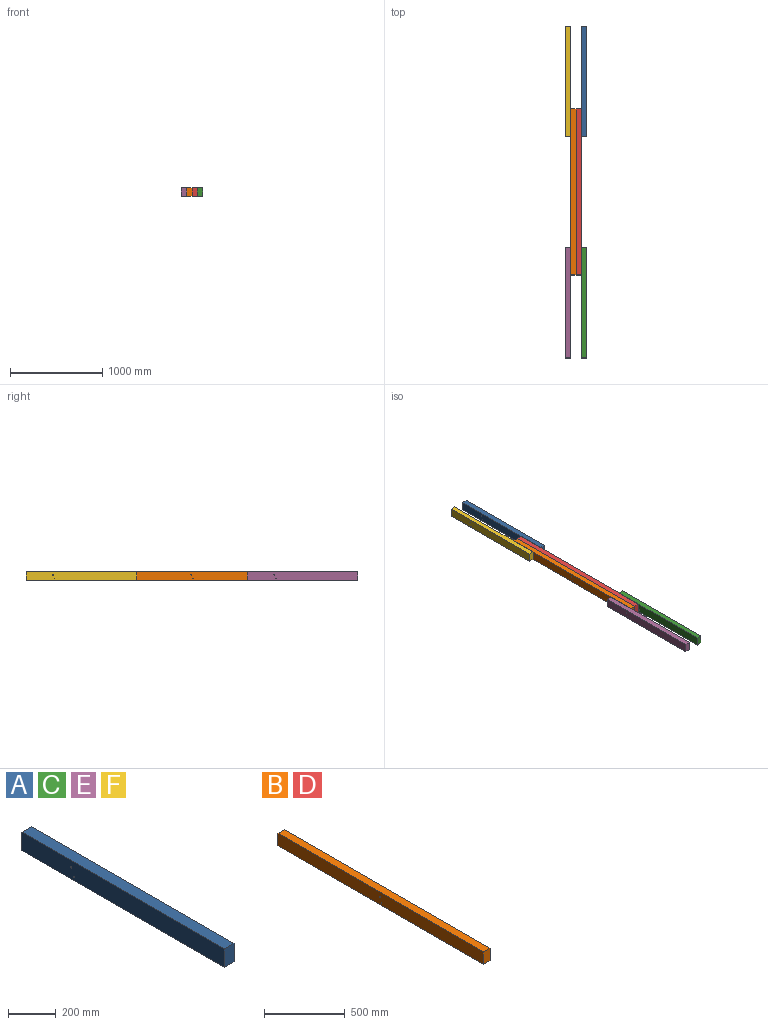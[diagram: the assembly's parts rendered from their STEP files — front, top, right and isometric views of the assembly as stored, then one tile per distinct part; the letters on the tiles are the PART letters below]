
ASSEMBLY  parts=6 mates=5
PART A: 8 faces, bbox 58x1200x95 mm
  f0: plane 1200x58mm, normal (0,0,-1), area 69600mm2, adj f1,f3,f4,f5
  f1: plane 1200x95mm, normal (1,0,0), area 113943.5mm2, adj f0,f2,f4,f5,f6,f7
  f2: plane 1200x58mm, normal (0,0,1), area 69600mm2, adj f1,f3,f4,f5
  f3: plane 1200x95mm, normal (-1,0,0), area 113943.5mm2, adj f0,f2,f4,f5,f6,f7
  f4: plane 95x58mm, normal (0,-1,0), area 5510mm2, adj f0,f1,f2,f3
  f5: plane 95x58mm, normal (0,1,0), area 5510mm2, adj f0,f1,f2,f3
  f6: cylinder r=3mm len=58mm, axis (1,0,0), area 1093.3mm2, adj f1,f3
  f7: cylinder r=3mm len=58mm, axis (1,0,0), area 1093.3mm2, adj f1,f3
PART B: 8 faces, bbox 58x1800x95 mm
  f0: plane 1800x58mm, normal (0,0,-1), area 104400mm2, adj f1,f3,f4,f5
  f1: plane 1800x95mm, normal (1,0,0), area 170943.5mm2, adj f0,f2,f4,f5,f6,f7
  f2: plane 1800x58mm, normal (0,0,1), area 104400mm2, adj f1,f3,f4,f5
  f3: plane 1800x95mm, normal (-1,0,0), area 170943.5mm2, adj f0,f2,f4,f5,f6,f7
  f4: plane 95x58mm, normal (0,-1,0), area 5510mm2, adj f0,f1,f2,f3
  f5: plane 95x58mm, normal (0,1,0), area 5510mm2, adj f0,f1,f2,f3
  f6: cylinder r=3mm len=58mm, axis (1,0,0), area 1093.3mm2, adj f1,f3
  f7: cylinder r=3mm len=58mm, axis (1,0,0), area 1093.3mm2, adj f1,f3
PART C: same geometry as A
PART D: same geometry as B
PART E: same geometry as A
PART F: same geometry as A
PLACE A t=(233,900,0)mm
PLACE B t=(117,0,0)mm
PLACE C t=(233,-1500,0)mm
PLACE D t=(175,0,0)mm
PLACE E t=(59,-1500,0)mm
PLACE F t=(59,900,0)mm
MATE fastened E.f1 <-> B.f3  axis (1,0,0) through (88,-1500,47.5)mm
MATE fastened B.f1 <-> D.f3  axis (1,0,0) through (146,-1800,47.5)mm
MATE fastened F.f1 <-> B.f3  axis (1,0,0) through (88,-300,47.5)mm
MATE fastened A.f3 <-> D.f1  axis (-1,0,0) through (204,-300,47.5)mm
MATE fastened C.f3 <-> D.f1  axis (-1,0,0) through (204,-1500,47.5)mm
